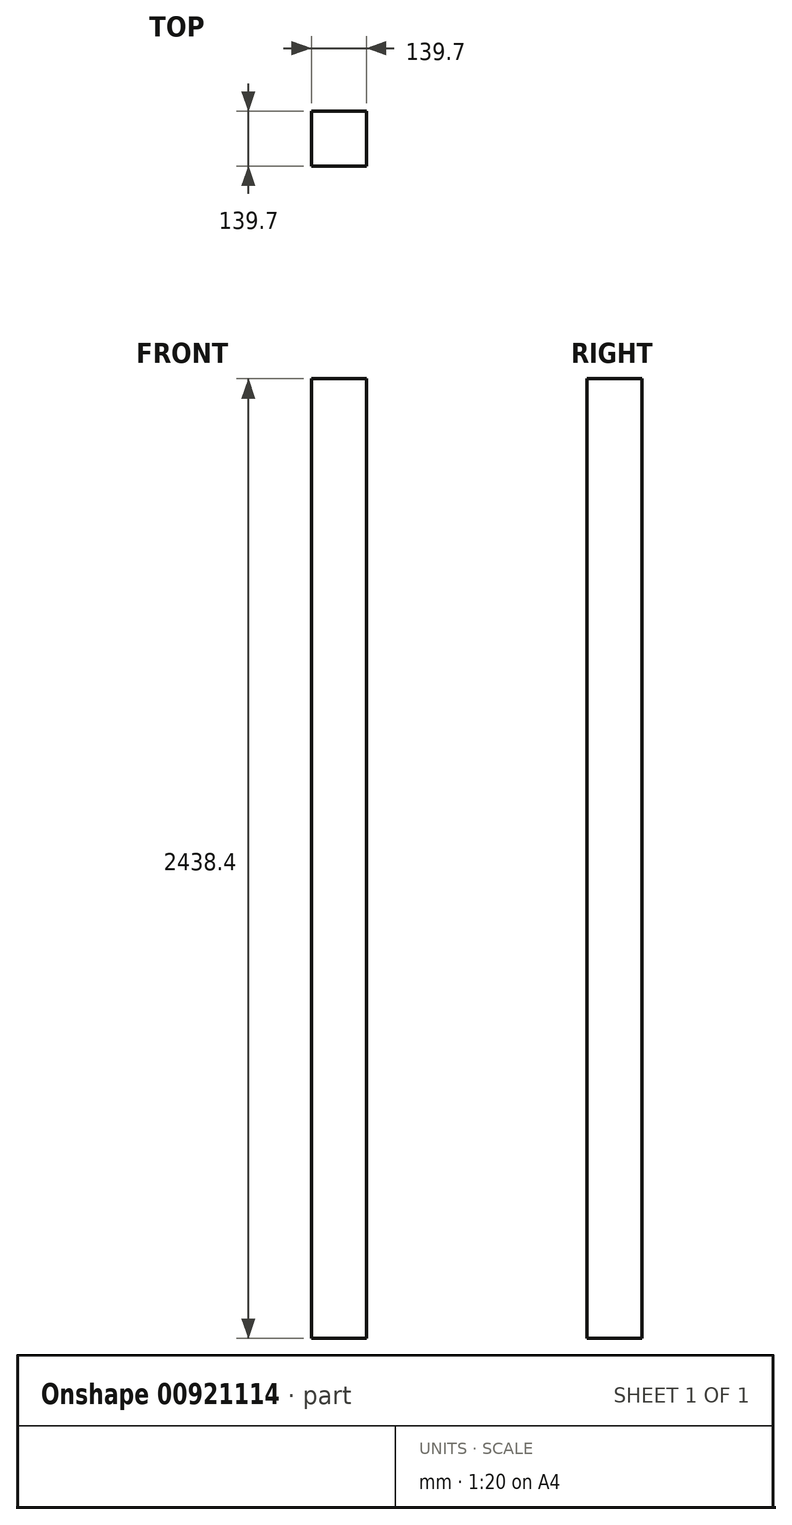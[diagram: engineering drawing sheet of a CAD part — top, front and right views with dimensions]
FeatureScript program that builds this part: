
annotation { "Feature Type Name" : "Feature", "Feature Type Description" : "" }
export const myFeature = defineFeature(function(context is Context, id is Id, definition is map)
    precondition{}
    {
        {
            var Q0;
            Q0=qCreatedBy(makeId("Top.planeOp"),FACE);
            var sketch = newSketch(context, id + "F0", { "sketchPlane" : qUnion([Q0])});
            skLineSegment(sketch, "E0.bottom", {"start": v(0, 40.07) * mm, "end": v(139.7, 40.07) * mm});
            skLineSegment(sketch, "E0.top", {"start": v(0, -99.63) * mm, "end": v(139.7, -99.63) * mm});
            skLineSegment(sketch, "E0.left", {"start": v(0, 40.07) * mm, "end": v(0, -99.63) * mm});
            skLineSegment(sketch, "E0.right", {"start": v(139.7, 40.07) * mm, "end": v(139.7, -99.63) * mm});
            skSolve(sketch);
        }
        {
            var Q0;
            Q0 = qSketchRegion(id + "F0", true);
            extrude(context, id + "F1", {"entities" : qUnion([Q0]), "depth" : 2438.4 * mm, "offsetDistance" : 25.4 * mm});
        }
    });
